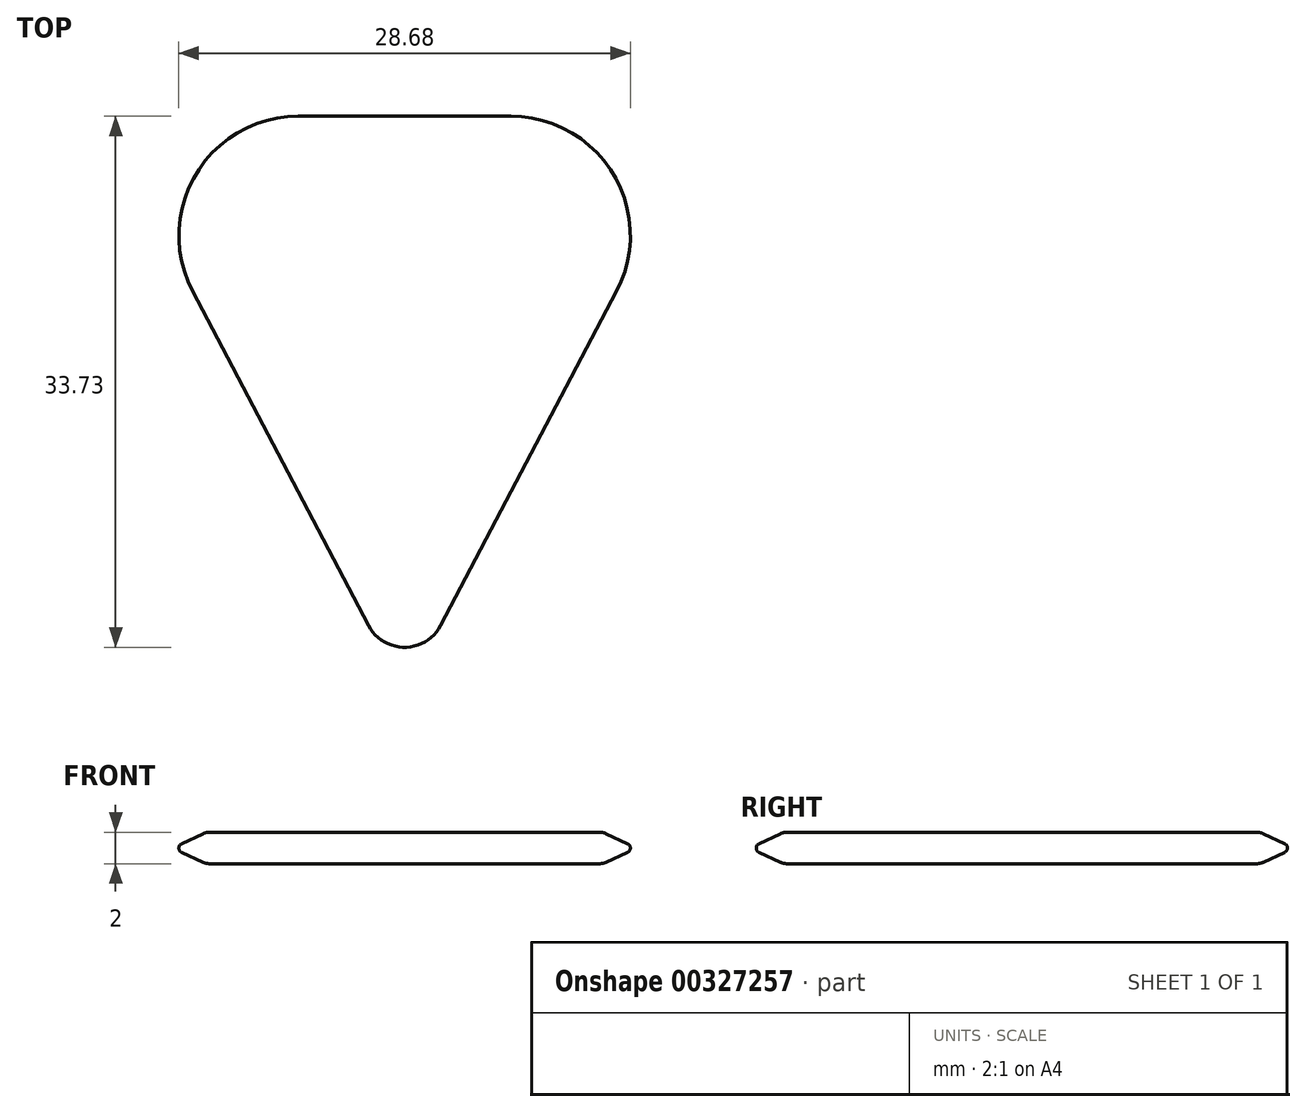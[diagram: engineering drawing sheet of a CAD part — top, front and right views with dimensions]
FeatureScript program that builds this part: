
annotation { "Feature Type Name" : "Feature", "Feature Type Description" : "" }
export const myFeature = defineFeature(function(context is Context, id is Id, definition is map)
    precondition{}
    {
        {
            var Q0;
            Q0=qCreatedBy(makeId("Top.planeOp"),FACE);
            var sketch = newSketch(context, id + "F0", { "sketchPlane" : qUnion([Q0])});
            skLineSegment(sketch, "E0", {"start": v(-6.75, 12.45) * mm, "end": v(6.75, 12.45) * mm});
            skLineSegment(sketch, "E1", {"start": v(13.83, 0.73) * mm, "end": v(2.65, -20.5) * mm});
            skLineSegment(sketch, "E2", {"start": v(-2.65, -20.5) * mm, "end": v(-13.83, 0.73) * mm});
            skPoint(sketch, "E3.visualSharp", {"position": v(-20, 12.45) * mm});
            skArc(sketch, "E3.filletArc", {"start": v(-6.75, 12.45) * mm, "mid": v(-13.6, 8.59) * mm, "end": v(-13.83, 0.73) * mm});
            skPoint(sketch, "E4.visualSharp", {"position": v(20, 12.45) * mm});
            skArc(sketch, "E4.filletArc", {"start": v(13.83, 0.73) * mm, "mid": v(13.6, 8.59) * mm, "end": v(6.75, 12.45) * mm});
            skPoint(sketch, "E5.visualSharp", {"position": v(0, -25.55) * mm});
            skArc(sketch, "E5.filletArc", {"start": v(-2.65, -20.5) * mm, "mid": v(0, -22.1) * mm, "end": v(2.65, -20.5) * mm});
            skSolve(sketch);
        }
        {
            var Q0;
            Q0=makeQuery(id+"F0.imprint","IMPRINT",FACE,{"disambiguationData":[TD([[makeQuery(id+"F0.imprint","IMPRINT",EDGE,{"derivedFrom":sQuery(id+"F0.wireOp",EDGE,"E0")}),-1.0]])]});
            extrude(context, id + "F1", {"entities" : qUnion([Q0]), "endBound" : BoundingType.SYMMETRIC, "depth" : 2 * mm});
        }
        {
            var Q0;
            Q0=makeQuery(id+"F1.opExtrude","CAP_EDGE",EDGE,{"disambiguationData":[OSD([sQuery(id+"F0.wireOp",EDGE,"E1")])],"isStart":false});
            var Q1;
            Q1=makeQuery(id+"F1.opExtrude","CAP_EDGE",EDGE,{"disambiguationData":[OSD([sQuery(id+"F0.wireOp",EDGE,"E1")])],"isStart":true});
            chamfer(context, id + "F2", {"entities" : qUnion([Q0, Q1]), "chamferType" : ChamferType.OFFSET_ANGLE, "width" : 1 * mm, "oppositeDirection" : false, "angle" : 65 * degree, "tangentPropagation" : true});
        }
        {
            var Q0;
            {var subQ0=sQuery(id+"F0.wireOp",EDGE,"E2");Q0=makeQuery(id+"F2.opChamfer","BLEND_EDGE",EDGE,{"blendedFrom":[makeQuery(id+"F1.opExtrude","CAP_EDGE",EDGE,{"disambiguationData":[OSD([subQ0])],"isStart":false}),makeQuery(id+"F1.opExtrude","CAP_FACE",FACE,{"disambiguationData":[OSD([sQuery(id+"F0.wireOp",EDGE,"E0"),sQuery(id+"F0.wireOp",EDGE,"E1"),subQ0,sQuery(id+"F0.wireOp",EDGE,"E3.filletArc"),sQuery(id+"F0.wireOp",EDGE,"E4.filletArc"),sQuery(id+"F0.wireOp",EDGE,"E5.filletArc")])],"isStart":false})],"blendedInto":[makeQuery(id+"F1.opExtrude","CAP_FACE",FACE,{"disambiguationData":[OSD([sQuery(id+"F0.wireOp",EDGE,"E0"),sQuery(id+"F0.wireOp",EDGE,"E1"),subQ0,sQuery(id+"F0.wireOp",EDGE,"E3.filletArc"),sQuery(id+"F0.wireOp",EDGE,"E4.filletArc"),sQuery(id+"F0.wireOp",EDGE,"E5.filletArc")])],"isStart":false})]});}
            var Q1;
            {var subQ0=sQuery(id+"F0.wireOp",EDGE,"E1");Q1=makeQuery(id+"F2.opChamfer","BLEND_EDGE",EDGE,{"blendedFrom":[makeQuery(id+"F1.opExtrude","CAP_EDGE",EDGE,{"disambiguationData":[OSD([subQ0])],"isStart":true}),makeQuery(id+"F1.opExtrude","CAP_FACE",FACE,{"disambiguationData":[OSD([sQuery(id+"F0.wireOp",EDGE,"E0"),subQ0,sQuery(id+"F0.wireOp",EDGE,"E2"),sQuery(id+"F0.wireOp",EDGE,"E3.filletArc"),sQuery(id+"F0.wireOp",EDGE,"E4.filletArc"),sQuery(id+"F0.wireOp",EDGE,"E5.filletArc")])],"isStart":true})],"blendedInto":[makeQuery(id+"F1.opExtrude","CAP_FACE",FACE,{"disambiguationData":[OSD([sQuery(id+"F0.wireOp",EDGE,"E0"),subQ0,sQuery(id+"F0.wireOp",EDGE,"E2"),sQuery(id+"F0.wireOp",EDGE,"E3.filletArc"),sQuery(id+"F0.wireOp",EDGE,"E4.filletArc"),sQuery(id+"F0.wireOp",EDGE,"E5.filletArc")])],"isStart":true})]});}
            fillet(context, id + "F3", {"entities" : qUnion([Q0, Q1]), "radius" : 1 * mm, "tangentPropagation" : true, "allowEdgeOverflow" : false});
        }
        {
            var Q0;
            {var subQ0=sQuery(id+"F0.wireOp",EDGE,"E2");Q0=makeQuery(id+"F2.opChamfer","BLEND_EDGE",EDGE,{"blendedFrom":[makeQuery(id+"F1.opExtrude","CAP_EDGE",EDGE,{"disambiguationData":[OSD([subQ0])],"isStart":true}),makeQuery(id+"F1.opExtrude","CAP_EDGE",EDGE,{"disambiguationData":[OSD([subQ0])],"isStart":false})],"blendedInto":[]});}
            fillet(context, id + "F5", {"entities" : qUnion([Q0]), "radius" : 0.3 * mm, "tangentPropagation" : true, "allowEdgeOverflow" : false});
        }
    });
